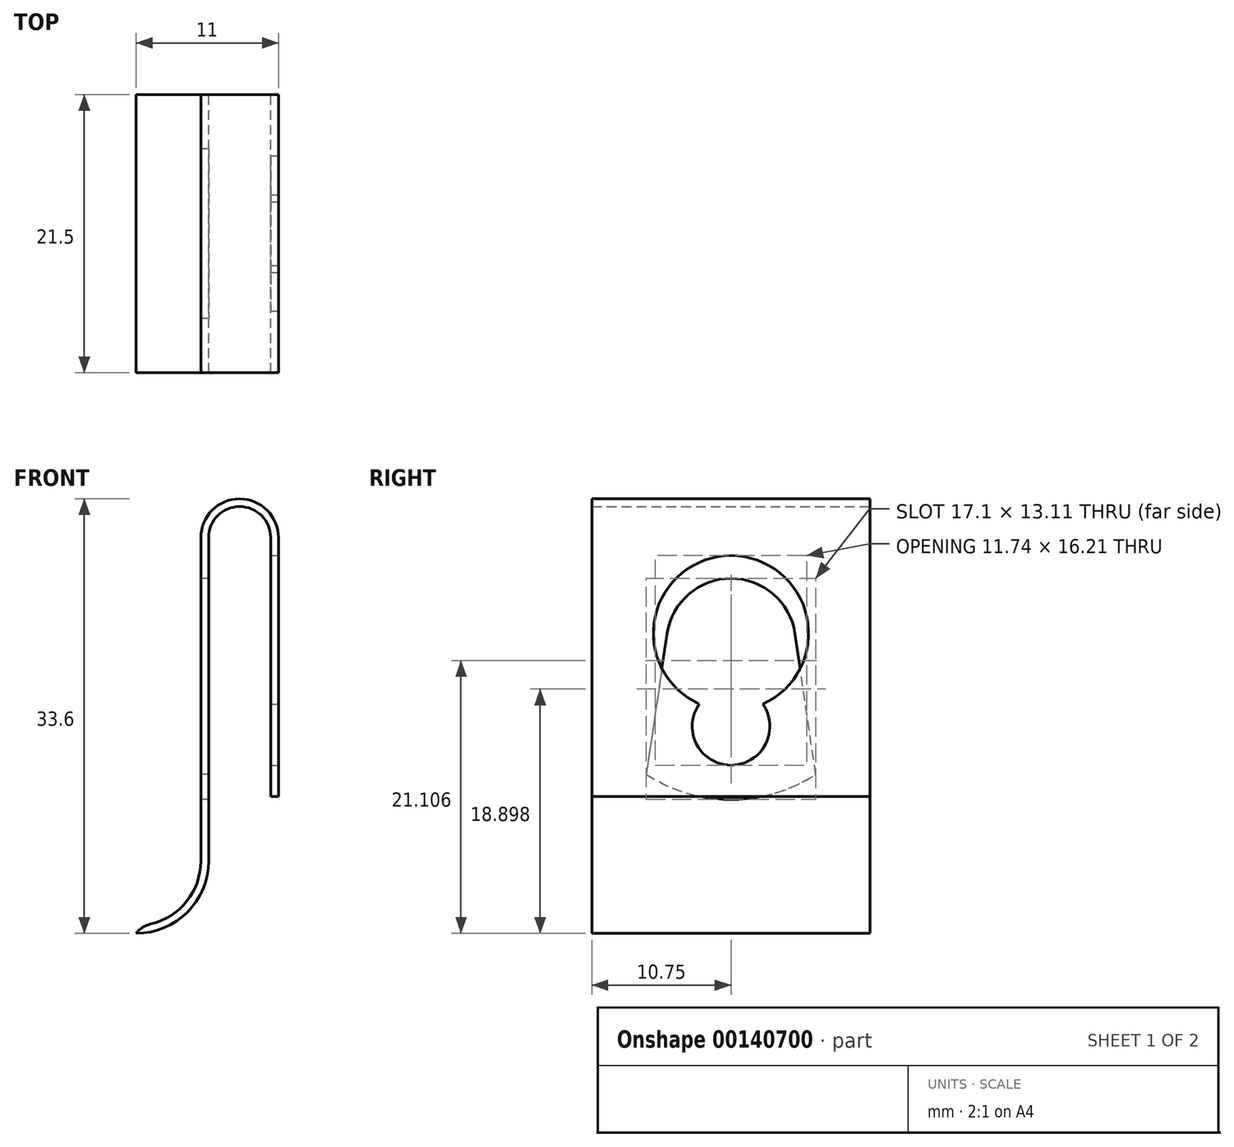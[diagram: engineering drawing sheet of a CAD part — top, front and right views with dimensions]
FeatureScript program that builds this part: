
annotation { "Feature Type Name" : "Feature", "Feature Type Description" : "" }
export const myFeature = defineFeature(function(context is Context, id is Id, definition is map)
    precondition{}
    {
        {
            var Q0;
            Q0=qCreatedBy(makeId("Front.planeOp"),FACE);
            var sketch = newSketch(context, id + "F0", { "sketchPlane" : qUnion([Q0])});
            skLineSegment(sketch, "E0", {"start": v(-3, -25) * mm, "end": v(-3, 0) * mm});
            skLineSegment(sketch, "E1", {"start": v(3, 0) * mm, "end": v(3, -20) * mm});
            skArc(sketch, "E2", {"start": v(3, 0) * mm, "mid": v(0, 3) * mm, "end": v(-3, 0) * mm});
            skArc(sketch, "E3", {"start": v(-8, -30) * mm, "mid": v(-4.46, -28.54) * mm, "end": v(-3, -25) * mm});
            skLineSegment(sketch, "E4.0", {"start": v(2.4, 0) * mm, "end": v(2.4, -20) * mm});
            skArc(sketch, "E4.1", {"start": v(2.4, 0) * mm, "mid": v(0, 2.4) * mm, "end": v(-2.4, 0) * mm});
            skLineSegment(sketch, "E4.2", {"start": v(-2.4, -25) * mm, "end": v(-2.4, 0) * mm});
            skArc(sketch, "E4.3", {"start": v(-8, -30.6) * mm, "mid": v(-4.04, -28.96) * mm, "end": v(-2.4, -25) * mm});
            skLineSegment(sketch, "E5", {"start": v(-8, -30.6) * mm, "end": v(-8, -30) * mm});
            skLineSegment(sketch, "E6", {"start": v(2.4, -20) * mm, "end": v(3, -20) * mm});
            skSolve(sketch);
        }
        {
            var Q0;
            Q0=makeQuery(id+"F0.imprint","IMPRINT",FACE,{"disambiguationData":[TD([[makeQuery(id+"F0.imprint","IMPRINT",EDGE,{"derivedFrom":sQuery(id+"F0.wireOp",EDGE,"E0")}),-1.0]])]});
            extrude(context, id + "F1", {"entities" : qUnion([Q0]), "depth" : 21.5 * mm});
        }
        {
            var Q0;
            Q0=makeQuery(id+"F1.opExtrude","SWEPT_FACE",FACE,{"disambiguationData":[OSD([sQuery(id+"F0.wireOp",EDGE,"E0")])]});
            var sketch = newSketch(context, id + "F2", { "sketchPlane" : qUnion([Q0])});
            skLineSegment(sketch, "E7", {"start": v(4.2, -18.3) * mm, "end": v(5.8, -7.42) * mm});
            skLineSegment(sketch, "E8", {"start": v(15.7, -7.42) * mm, "end": v(17.3, -18.3) * mm});
            skArc(sketch, "E9", {"start": v(15.7, -7.42) * mm, "mid": v(10.75, -3.15) * mm, "end": v(5.8, -7.42) * mm});
            skArc(sketch, "E10", {"start": v(4.2, -18.3) * mm, "mid": v(10.75, -20.25) * mm, "end": v(17.3, -18.3) * mm});
            skSolve(sketch);
        }
        {
            var Q0;
            Q0=makeQuery(id+"F2.imprint","IMPRINT",FACE,{"disambiguationData":[TD([[makeQuery(id+"F2.imprint","IMPRINT",EDGE,{"derivedFrom":sQuery(id+"F2.wireOp",EDGE,"E7")}),-1.0]])]});
            extrude(context, id + "F3", {"entities" : qUnion([Q0]), "operationType" : NewBodyOperationType.REMOVE, "oppositeDirection" : true, "depth" : 1 * mm});
        }
        {
            var Q0;
            Q0=makeQuery(id+"F1.opExtrude","SWEPT_FACE",FACE,{"disambiguationData":[OSD([sQuery(id+"F0.wireOp",EDGE,"E1")])]});
            var sketch = newSketch(context, id + "F4", { "sketchPlane" : qUnion([Q0])});
            skArc(sketch, "E11", {"start": v(-8.3, -12.87) * mm, "mid": v(-10.75, -1.4) * mm, "end": v(-13.2, -12.87) * mm});
            skArc(sketch, "E12", {"start": v(-13.2, -12.87) * mm, "mid": v(-10.75, -17.6) * mm, "end": v(-8.3, -12.87) * mm});
            skLineSegment(sketch, "E13", {"start": v(-10.75, 0) * mm, "end": v(-10.75, -20) * mm, "construction": true});
            skSolve(sketch);
        }
        {
            var Q0;
            Q0=makeQuery(id+"F4.imprint","IMPRINT",FACE,{"disambiguationData":[TD([[makeQuery(id+"F4.imprint","IMPRINT",EDGE,{"derivedFrom":sQuery(id+"F4.wireOp",EDGE,"E11")}),1.0]])]});
            extrude(context, id + "F5", {"entities" : qUnion([Q0]), "operationType" : NewBodyOperationType.REMOVE, "oppositeDirection" : true, "depth" : 1 * mm});
        }
        {
            var Q0;
            Q0=makeQuery(id+"F1.opExtrude","SWEPT_EDGE",EDGE,{"disambiguationData":[OSD([sQuery(id+"F0.wireOp",EDGE,"E3"),sQuery(id+"F0.wireOp",EDGE,"E5")])]});
            fillet(context, id + "F6", {"entities" : qUnion([Q0]), "radius" : 2 * mm, "tangentPropagation" : true, "allowEdgeOverflow" : false});
        }
    });
